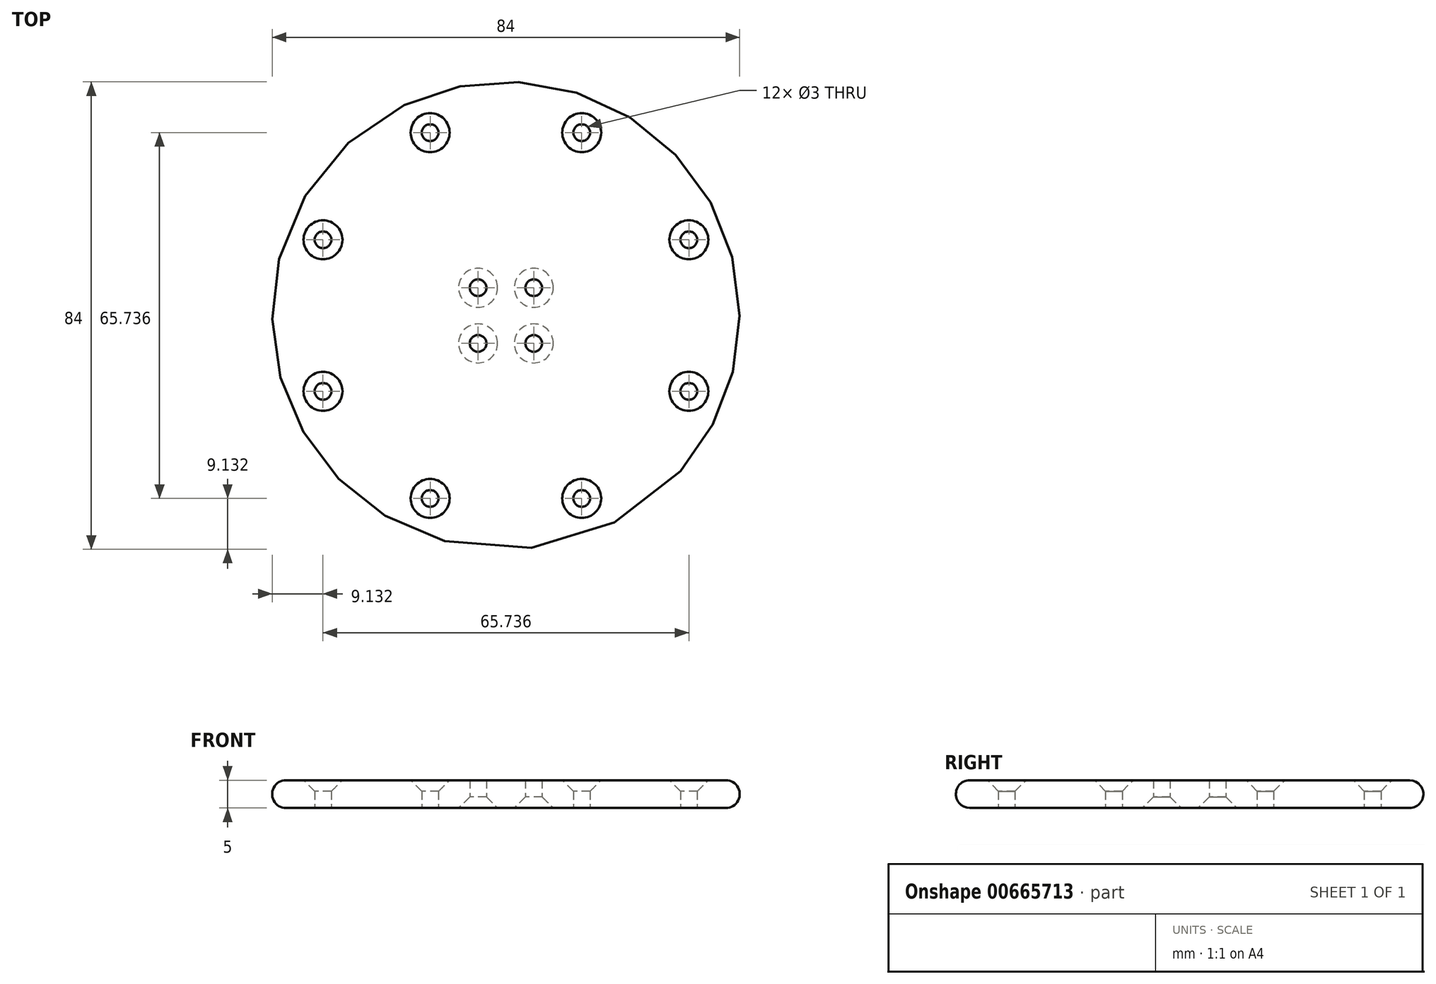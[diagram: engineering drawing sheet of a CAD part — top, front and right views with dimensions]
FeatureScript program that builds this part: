
annotation { "Feature Type Name" : "Feature", "Feature Type Description" : "" }
export const myFeature = defineFeature(function(context is Context, id is Id, definition is map)
    precondition{}
    {
        {
            var Q0;
            Q0=qCreatedBy(makeId("Top.planeOp"),FACE);
            var sketch = newSketch(context, id + "F0", { "sketchPlane" : qUnion([Q0])});
            skCircle(sketch, "E0", {"center": v(0, 0) * mm, "radius": 12.5 * mm, "construction": true});
            skCircle(sketch, "E1", {"center": v(0, 0) * mm, "radius": 23.5 * mm, "construction": true});
            skLineSegment(sketch, "E2.bottom", {"start": v(36.5, -36.5) * mm, "end": v(-36.5, -36.5) * mm, "construction": true});
            skLineSegment(sketch, "E2.top", {"start": v(36.5, 36.5) * mm, "end": v(-36.5, 36.5) * mm, "construction": true});
            skLineSegment(sketch, "E2.left", {"start": v(36.5, -36.5) * mm, "end": v(36.5, 36.5) * mm, "construction": true});
            skLineSegment(sketch, "E2.right", {"start": v(-36.5, -36.5) * mm, "end": v(-36.5, 36.5) * mm, "construction": true});
            skLineSegment(sketch, "E3.bottom", {"start": v(28.5, -28.5) * mm, "end": v(-28.5, -28.5) * mm, "construction": true});
            skLineSegment(sketch, "E3.top", {"start": v(28.5, 28.5) * mm, "end": v(-28.5, 28.5) * mm, "construction": true});
            skLineSegment(sketch, "E3.left", {"start": v(28.5, -28.5) * mm, "end": v(28.5, 28.5) * mm, "construction": true});
            skLineSegment(sketch, "E3.right", {"start": v(-28.5, -28.5) * mm, "end": v(-28.5, 28.5) * mm, "construction": true});
            skCircle(sketch, "E4", {"center": v(-28.5, 28.5) * mm, "radius": 3 * mm, "construction": true});
            skCircle(sketch, "E5", {"center": v(28.5, 28.5) * mm, "radius": 3 * mm, "construction": true});
            skCircle(sketch, "E6", {"center": v(28.5, -28.5) * mm, "radius": 3 * mm, "construction": true});
            skCircle(sketch, "E7", {"center": v(-28.5, -28.5) * mm, "radius": 3 * mm, "construction": true});
            skCircle(sketch, "E8", {"center": v(0, 0) * mm, "radius": 17.5 * mm, "construction": true});
            skCircle(sketch, "E9", {"center": v(0, 0) * mm, "radius": 15 * mm, "construction": true});
            skCircle(sketch, "E10", {"center": v(-28.5, 28.5) * mm, "radius": 8 * mm, "construction": true});
            skCircle(sketch, "E11", {"center": v(28.5, 28.5) * mm, "radius": 8 * mm, "construction": true});
            skCircle(sketch, "E12", {"center": v(28.5, -28.5) * mm, "radius": 8 * mm, "construction": true});
            skCircle(sketch, "E13", {"center": v(-28.5, -28.5) * mm, "radius": 8 * mm, "construction": true});
            skLineSegment(sketch, "E14.bottom", {"start": v(5, -5) * mm, "end": v(-5, -5) * mm, "construction": true});
            skLineSegment(sketch, "E14.top", {"start": v(5, 5) * mm, "end": v(-5, 5) * mm, "construction": true});
            skLineSegment(sketch, "E14.left", {"start": v(5, -5) * mm, "end": v(5, 5) * mm, "construction": true});
            skLineSegment(sketch, "E14.right", {"start": v(-5, -5) * mm, "end": v(-5, 5) * mm, "construction": true});
            skCircle(sketch, "E15", {"center": v(-5, 5) * mm, "radius": 1.5 * mm});
            skCircle(sketch, "E16", {"center": v(5, 5) * mm, "radius": 1.5 * mm});
            skCircle(sketch, "E17", {"center": v(5, -5) * mm, "radius": 1.5 * mm});
            skCircle(sketch, "E18", {"center": v(-5, -5) * mm, "radius": 1.5 * mm});
            skCircle(sketch, "E19", {"center": v(0, 0) * mm, "radius": 42 * mm});
            skCircle(sketch, "E20.cCircle", {"center": v(0, 0) * mm, "radius": 32.87 * mm, "construction": true});
            skLineSegment(sketch, "E20.0", {"start": v(32.87, 13.61) * mm, "end": v(32.87, -13.61) * mm});
            skLineSegment(sketch, "E20.1", {"start": v(32.87, -13.61) * mm, "end": v(13.61, -32.87) * mm});
            skLineSegment(sketch, "E20.2", {"start": v(13.61, -32.87) * mm, "end": v(-13.61, -32.87) * mm});
            skLineSegment(sketch, "E20.3", {"start": v(-13.61, -32.87) * mm, "end": v(-32.87, -13.61) * mm});
            skLineSegment(sketch, "E20.4", {"start": v(-32.87, -13.61) * mm, "end": v(-32.87, 13.61) * mm});
            skLineSegment(sketch, "E20.5", {"start": v(-32.87, 13.61) * mm, "end": v(-13.61, 32.87) * mm});
            skLineSegment(sketch, "E20.6", {"start": v(-13.61, 32.87) * mm, "end": v(13.61, 32.87) * mm});
            skLineSegment(sketch, "E20.7", {"start": v(13.61, 32.87) * mm, "end": v(32.87, 13.61) * mm});
            skPoint(sketch, "E20.0.midPoint", {"position": v(32.87, 0) * mm});
            skCircle(sketch, "E21", {"center": v(-13.61, -32.87) * mm, "radius": 1.5 * mm});
            skCircle(sketch, "E22", {"center": v(13.61, -32.87) * mm, "radius": 1.5 * mm});
            skCircle(sketch, "E23", {"center": v(32.87, -13.61) * mm, "radius": 1.5 * mm});
            skCircle(sketch, "E24", {"center": v(32.87, 13.61) * mm, "radius": 1.5 * mm});
            skCircle(sketch, "E25", {"center": v(-13.61, 32.87) * mm, "radius": 1.5 * mm});
            skCircle(sketch, "E26", {"center": v(13.61, 32.87) * mm, "radius": 1.5 * mm});
            skCircle(sketch, "E27", {"center": v(-32.87, 13.61) * mm, "radius": 1.5 * mm});
            skCircle(sketch, "E28", {"center": v(-32.87, -13.61) * mm, "radius": 1.5 * mm});
            skSolve(sketch);
        }
        {
            var Q0;
            Q0=makeQuery(id+"F0.imprint","IMPRINT",FACE,{"disambiguationData":[TD([[makeQuery(id+"F0.imprint","IMPRINT",EDGE,{"derivedFrom":sQuery(id+"F0.wireOp",EDGE,"E15")}),-1.0]])]});
            var Q1;
            Q1=makeQuery(id+"F0.imprint","IMPRINT",FACE,{"disambiguationData":[TD([[makeQuery(id+"F0.imprint","IMPRINT",EDGE,{"derivedFrom":sQuery(id+"F0.wireOp",EDGE,"E19")}),1.0]])]});
            extrude(context, id + "F1", {"entities" : qUnion([Q0, Q1]), "depth" : 5 * mm, "offsetDistance" : 25 * mm});
        }
        {
            var Q0;
            Q0=makeQuery(id+"F1.opExtrude","SWEPT_FACE",FACE,{"disambiguationData":[OSD([sQuery(id+"F0.wireOp",EDGE,"E19")])]});
            fillet(context, id + "F2", {"entities" : qUnion([Q0]), "radius" : 2.5 * mm, "tangentPropagation" : true, "allowEdgeOverflow" : false});
        }
        {
            var Q0;
            Q0=makeQuery(id+"F1.opExtrude","CAP_EDGE",EDGE,{"disambiguationData":[OSD([sQuery(id+"F0.wireOp",EDGE,"E27")])],"isStart":false});
            var Q1;
            Q1=makeQuery(id+"F1.opExtrude","CAP_EDGE",EDGE,{"disambiguationData":[OSD([sQuery(id+"F0.wireOp",EDGE,"E25")])],"isStart":false});
            var Q2;
            Q2=makeQuery(id+"F1.opExtrude","CAP_EDGE",EDGE,{"disambiguationData":[OSD([sQuery(id+"F0.wireOp",EDGE,"E26")])],"isStart":false});
            var Q3;
            Q3=makeQuery(id+"F1.opExtrude","CAP_EDGE",EDGE,{"disambiguationData":[OSD([sQuery(id+"F0.wireOp",EDGE,"E24")])],"isStart":false});
            var Q4;
            Q4=makeQuery(id+"F1.opExtrude","CAP_EDGE",EDGE,{"disambiguationData":[OSD([sQuery(id+"F0.wireOp",EDGE,"E23")])],"isStart":false});
            var Q5;
            Q5=makeQuery(id+"F1.opExtrude","CAP_EDGE",EDGE,{"disambiguationData":[OSD([sQuery(id+"F0.wireOp",EDGE,"E21")])],"isStart":false});
            var Q6;
            Q6=makeQuery(id+"F1.opExtrude","CAP_EDGE",EDGE,{"disambiguationData":[OSD([sQuery(id+"F0.wireOp",EDGE,"E22")])],"isStart":false});
            var Q7;
            Q7=makeQuery(id+"F1.opExtrude","CAP_EDGE",EDGE,{"disambiguationData":[OSD([sQuery(id+"F0.wireOp",EDGE,"E28")])],"isStart":false});
            var Q8;
            Q8=makeQuery(id+"F1.opExtrude","CAP_EDGE",EDGE,{"disambiguationData":[OSD([sQuery(id+"F0.wireOp",EDGE,"E18")])],"isStart":true});
            var Q9;
            Q9=makeQuery(id+"F1.opExtrude","CAP_EDGE",EDGE,{"disambiguationData":[OSD([sQuery(id+"F0.wireOp",EDGE,"E15")])],"isStart":true});
            var Q10;
            Q10=makeQuery(id+"F1.opExtrude","CAP_EDGE",EDGE,{"disambiguationData":[OSD([sQuery(id+"F0.wireOp",EDGE,"E16")])],"isStart":true});
            var Q11;
            Q11=makeQuery(id+"F1.opExtrude","CAP_EDGE",EDGE,{"disambiguationData":[OSD([sQuery(id+"F0.wireOp",EDGE,"E17")])],"isStart":true});
            chamfer(context, id + "F3", {"entities" : qUnion([Q0, Q1, Q2, Q3, Q4, Q5, Q6, Q7, Q8, Q9, Q10, Q11]), "width" : 2 * mm, "tangentPropagation" : true});
        }
    });
